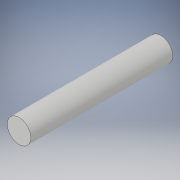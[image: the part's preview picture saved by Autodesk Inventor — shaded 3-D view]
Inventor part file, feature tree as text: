
AUTODESK INVENTOR PART (.ipt)
format: ipt  version: 2019.4 (Build 234330000, 330)  size: 90,112 bytes
history: native  units: mm
features: other x1, extrude x1, sketch x1
ambient origin geometry x8: Origin, YZ Plane, XZ Plane, XY Plane, X Axis, Y Axis, Z Axis, Center Point
bodies: Body1 (feature_tree)
feature tree (3):
  other  "Sólido1"
  extrude  "Extrusión1"  Depth=1500.0mm TaperAngle=0.0deg
  sketch  "Boceto1"  dims[d0=249.0mm d1=1500.0mm d2=0.0mm]
